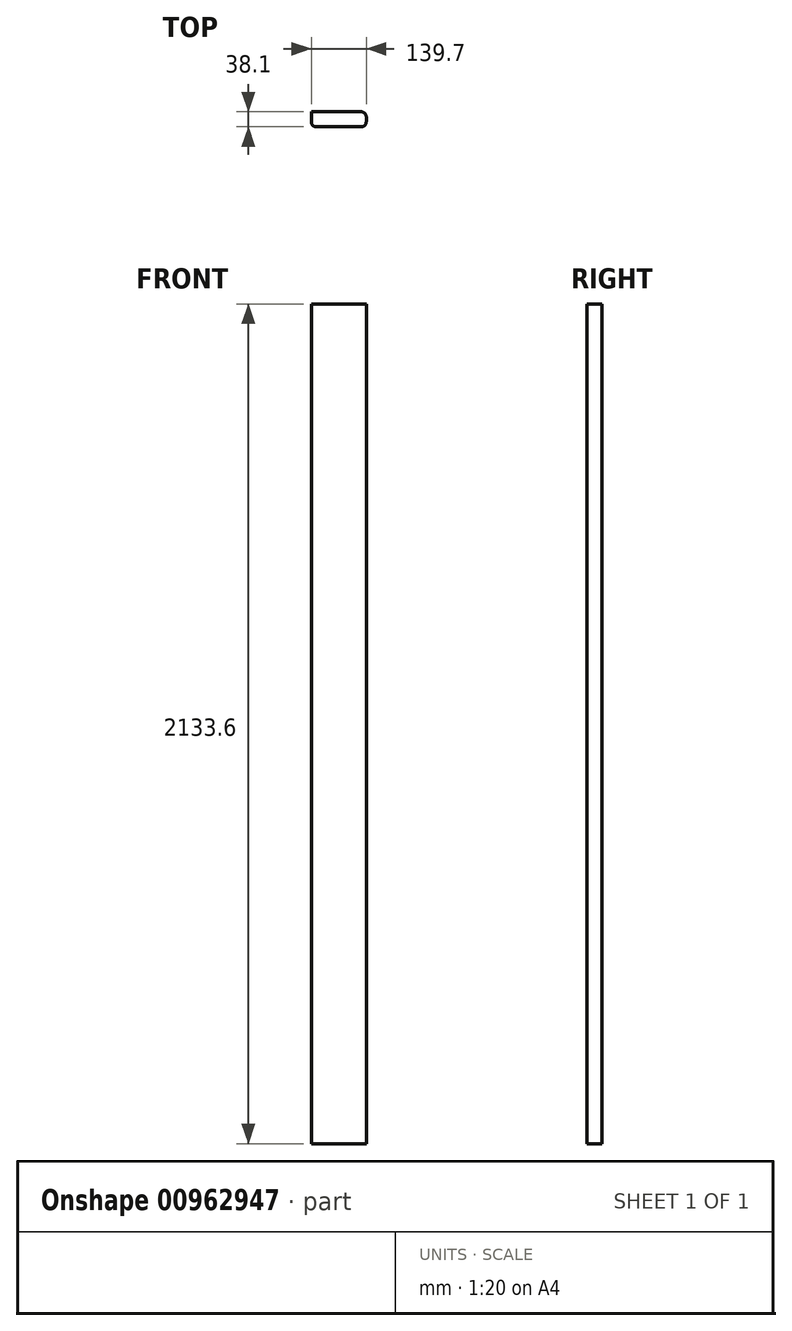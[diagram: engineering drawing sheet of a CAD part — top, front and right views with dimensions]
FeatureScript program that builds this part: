
annotation { "Feature Type Name" : "Feature", "Feature Type Description" : "" }
export const myFeature = defineFeature(function(context is Context, id is Id, definition is map)
    precondition{}
    {
        {
            var Q0;
            Q0=qCreatedBy(makeId("Top.planeOp"),FACE);
            var sketch = newSketch(context, id + "F0", { "sketchPlane" : qUnion([Q0])});
            skLineSegment(sketch, "E0.bottom", {"start": v(-76.7, -29.9) * mm, "end": v(63, -29.9) * mm});
            skLineSegment(sketch, "E0.top", {"start": v(-76.7, -68) * mm, "end": v(63, -68) * mm});
            skLineSegment(sketch, "E0.left", {"start": v(-76.7, -29.9) * mm, "end": v(-76.7, -68) * mm});
            skLineSegment(sketch, "E0.right", {"start": v(63, -29.9) * mm, "end": v(63, -68) * mm});
            skSolve(sketch);
        }
        {
            var Q0;
            Q0=makeQuery(id+"F0.imprint","IMPRINT",FACE,{"disambiguationData":[TD([[makeQuery(id+"F0.imprint","IMPRINT",EDGE,{"derivedFrom":sQuery(id+"F0.wireOp",EDGE,"E0.bottom")}),-1.0]])]});
            extrude(context, id + "F1", {"entities" : qUnion([Q0]), "depth" : 2133.6 * mm, "offsetDistance" : 25.4 * mm});
        }
        {
            var Q0;
            Q0=makeQuery(id+"F1.opExtrude","SWEPT_EDGE",EDGE,{"disambiguationData":[OSD([sQuery(id+"F0.wireOp",EDGE,"E0.top"),sQuery(id+"F0.wireOp",EDGE,"E0.left")])]});
            fillet(context, id + "F2", {"entities" : qUnion([Q0]), "radius" : 12.7 * mm, "tangentPropagation" : true, "allowEdgeOverflow" : false});
        }
        {
            var Q0;
            Q0=makeQuery(id+"F1.opExtrude","SWEPT_EDGE",EDGE,{"disambiguationData":[OSD([sQuery(id+"F0.wireOp",EDGE,"E0.top"),sQuery(id+"F0.wireOp",EDGE,"E0.right")])]});
            fillet(context, id + "F3", {"entities" : qUnion([Q0]), "radius" : 12.7 * mm, "tangentPropagation" : true, "allowEdgeOverflow" : false});
        }
        {
            var Q0;
            Q0=makeQuery(id+"F1.opExtrude","SWEPT_EDGE",EDGE,{"disambiguationData":[OSD([sQuery(id+"F0.wireOp",EDGE,"E0.bottom"),sQuery(id+"F0.wireOp",EDGE,"E0.right")])]});
            fillet(context, id + "F4", {"entities" : qUnion([Q0]), "radius" : 12.7 * mm, "tangentPropagation" : true, "allowEdgeOverflow" : false});
        }
    });
